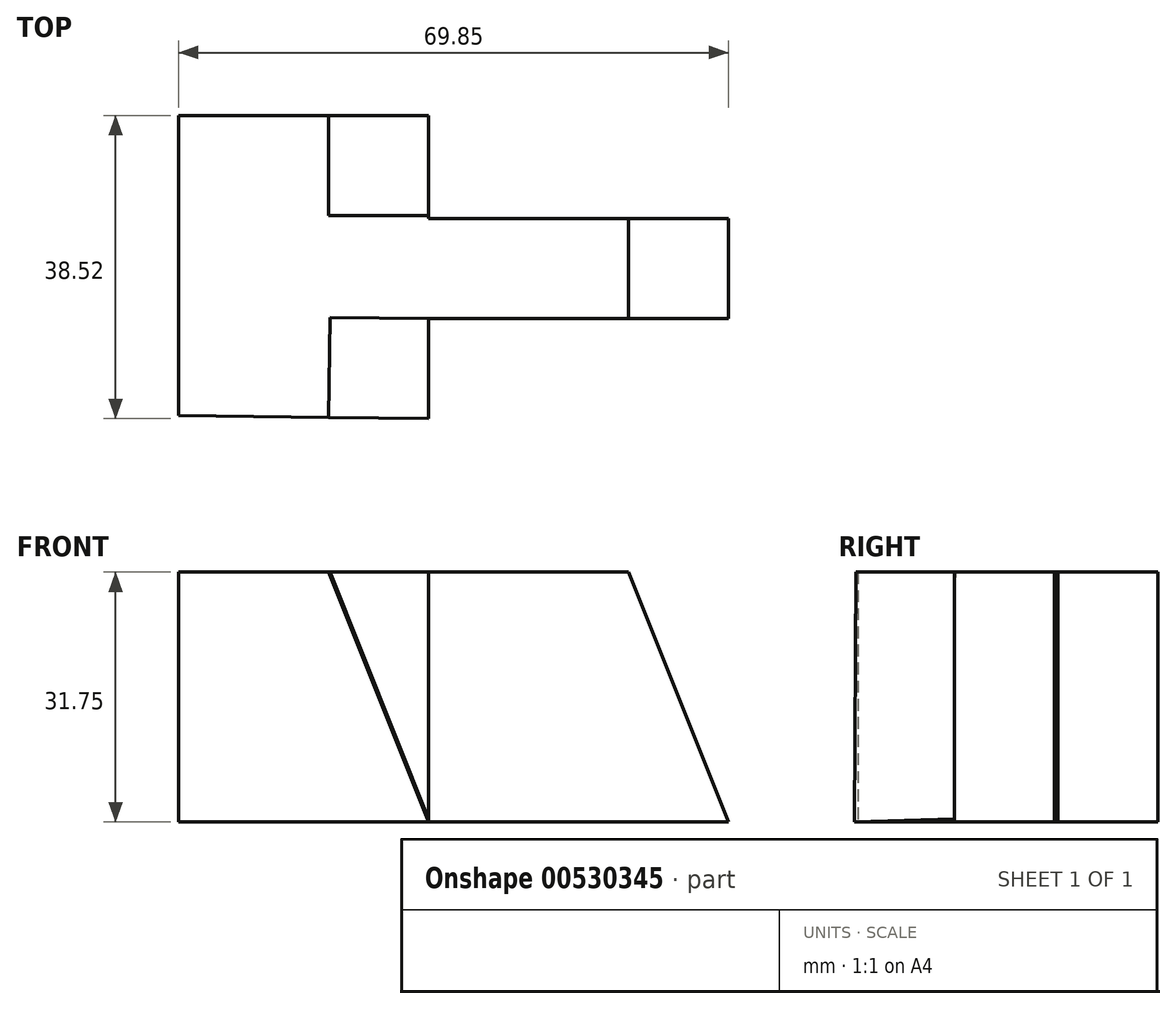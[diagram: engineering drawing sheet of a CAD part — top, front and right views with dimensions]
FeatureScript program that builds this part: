
annotation { "Feature Type Name" : "Feature", "Feature Type Description" : "" }
export const myFeature = defineFeature(function(context is Context, id is Id, definition is map)
    precondition{}
    {
        {
            var Q0;
            Q0=qCreatedBy(makeId("Top.planeOp"),FACE);
            var sketch = newSketch(context, id + "F0", { "sketchPlane" : qUnion([Q0])});
            skLineSegment(sketch, "E0", {"start": v(-76.48, 8) * mm, "end": v(-76.48, 46.1) * mm});
            skLineSegment(sketch, "E1", {"start": v(-76.48, 46.1) * mm, "end": v(-44.73, 46.1) * mm});
            skLineSegment(sketch, "E2", {"start": v(-44.73, 46.1) * mm, "end": v(-44.73, 32.97) * mm});
            skLineSegment(sketch, "E3", {"start": v(-44.73, 32.97) * mm, "end": v(-6.63, 32.97) * mm});
            skLineSegment(sketch, "E4", {"start": v(-6.63, 32.97) * mm, "end": v(-6.63, 20.27) * mm});
            skLineSegment(sketch, "E5", {"start": v(-6.63, 20.27) * mm, "end": v(-44.73, 20.27) * mm});
            skLineSegment(sketch, "E6", {"start": v(-44.73, 20.27) * mm, "end": v(-44.73, 7.57) * mm});
            skLineSegment(sketch, "E7", {"start": v(-44.73, 7.57) * mm, "end": v(-76.48, 8) * mm});
            skSolve(sketch);
        }
        {
            var Q0;
            Q0 = qSketchRegion(id + "F0", true);
            extrude(context, id + "F1", {"entities" : qUnion([Q0]), "depth" : 31.75 * mm, "offsetDistance" : 25.4 * mm});
        }
        {
            var Q0;
            Q0=makeQuery(id+"F1.opExtrude","SWEPT_FACE",FACE,{"disambiguationData":[OSD([sQuery(id+"F0.wireOp",EDGE,"E5")])]});
            var sketch = newSketch(context, id + "F2", { "sketchPlane" : qUnion([Q0])});
            skLineSegment(sketch, "E8", {"start": v(-19.33, 31.75) * mm, "end": v(-6.63, 0) * mm});
            skSolve(sketch);
        }
        {
            var Q0;
            Q0 = qSketchRegion(id + "F2", true);
            var Q1;
            {var subQ0=sQuery(id+"F2.wireOp",EDGE,"E8");Q1=makeQuery(id+"F2.imprint","IMPRINT",FACE,{"disambiguationData":[TD([[makeQuery(id+"F2.imprint","IMPRINT",EDGE,{"derivedFrom":subQ0}),1.0]])]});}
            extrude(context, id + "F3", {"entities" : qUnion([Q0, Q1]), "operationType" : NewBodyOperationType.REMOVE, "endBound" : BoundingType.THROUGH_ALL, "oppositeDirection" : true, "depth" : 25.4 * mm, "offsetDistance" : 25.4 * mm});
        }
        {
            var Q0;
            Q0=makeQuery(id+"F1.opExtrude","SWEPT_FACE",FACE,{"disambiguationData":[OSD([sQuery(id+"F0.wireOp",EDGE,"E7")])]});
            var sketch = newSketch(context, id + "F4", { "sketchPlane" : qUnion([Q0])});
            skLineSegment(sketch, "E9", {"start": v(-57.53, 31.75) * mm, "end": v(-44.83, 0) * mm});
            skSolve(sketch);
        }
        {
            var Q0;
            Q0 = qSketchRegion(id + "F4", true);
            var Q1;
            {var subQ0=sQuery(id+"F4.wireOp",EDGE,"E9");Q1=makeQuery(id+"F4.imprint","IMPRINT",FACE,{"disambiguationData":[TD([[makeQuery(id+"F4.imprint","IMPRINT",EDGE,{"derivedFrom":subQ0}),1.0]])]});}
            extrude(context, id + "F5", {"entities" : qUnion([Q0, Q1]), "operationType" : NewBodyOperationType.REMOVE, "oppositeDirection" : true, "depth" : 12.7 * mm, "offsetDistance" : 25.4 * mm});
        }
        {
            var Q0;
            Q0=makeQuery(id+"F1.opExtrude","SWEPT_FACE",FACE,{"disambiguationData":[OSD([sQuery(id+"F0.wireOp",EDGE,"E1")])]});
            var sketch = newSketch(context, id + "F6", { "sketchPlane" : qUnion([Q0])});
            skLineSegment(sketch, "E10", {"start": v(57.43, 31.75) * mm, "end": v(44.73, 0) * mm});
            skSolve(sketch);
        }
        {
            var Q0;
            Q0 = qSketchRegion(id + "F6", true);
            var Q1;
            {var subQ0=sQuery(id+"F6.wireOp",EDGE,"E10");Q1=makeQuery(id+"F6.imprint","IMPRINT",FACE,{"disambiguationData":[TD([[makeQuery(id+"F6.imprint","IMPRINT",EDGE,{"derivedFrom":subQ0}),-1.0]])]});}
            extrude(context, id + "F7", {"entities" : qUnion([Q0, Q1]), "operationType" : NewBodyOperationType.REMOVE, "oppositeDirection" : true, "depth" : 12.7 * mm, "offsetDistance" : 25.4 * mm});
        }
    });
